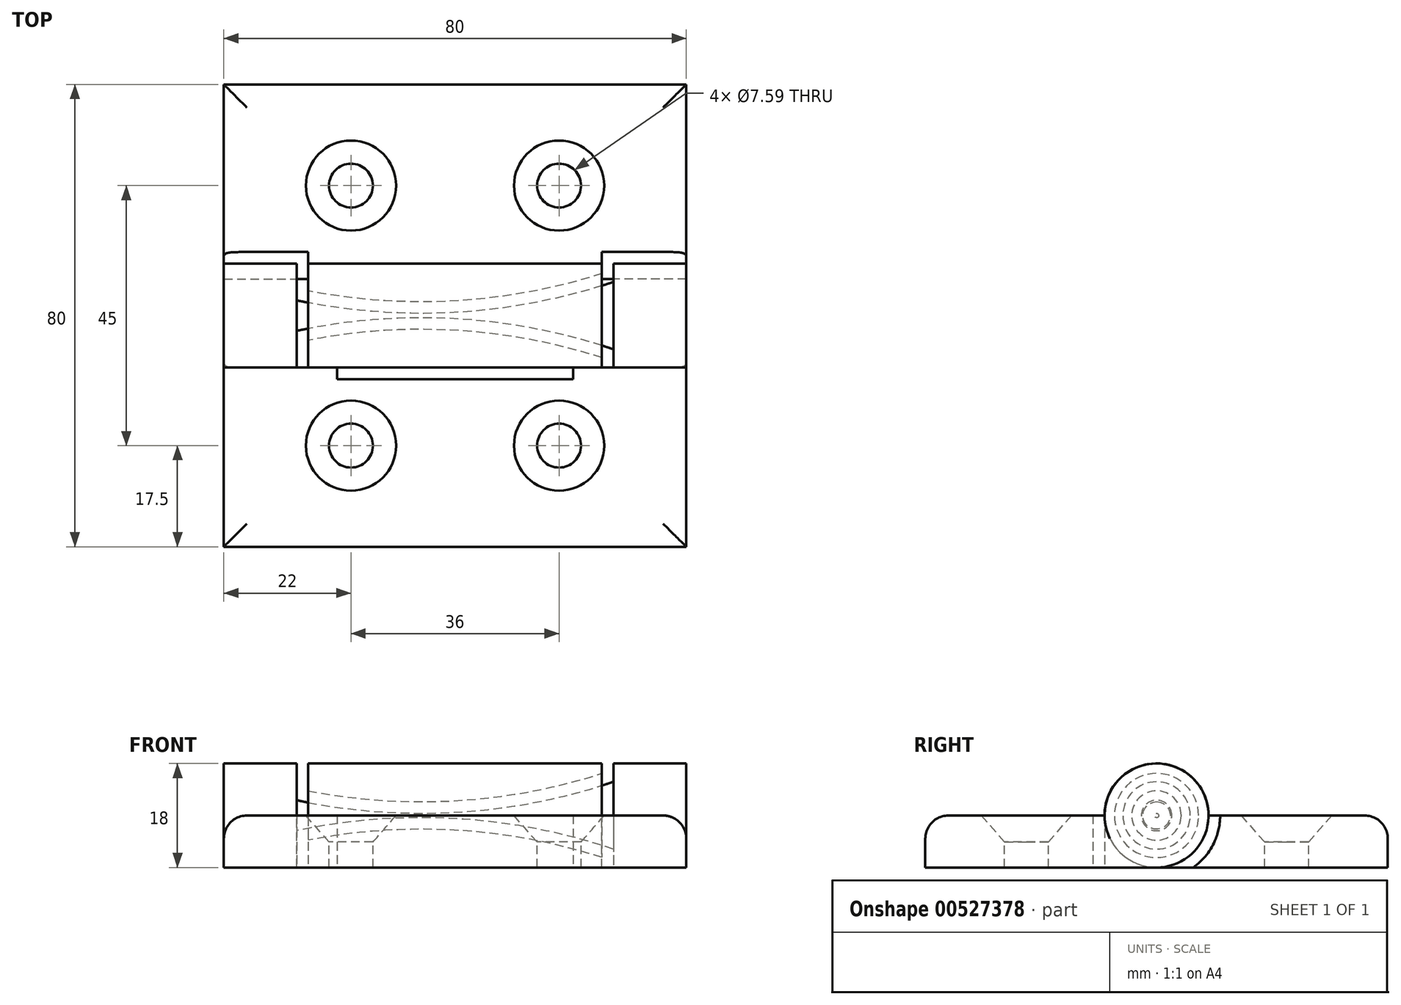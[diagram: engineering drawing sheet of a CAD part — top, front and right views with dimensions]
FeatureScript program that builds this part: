
annotation { "Feature Type Name" : "Feature", "Feature Type Description" : "" }
export const myFeature = defineFeature(function(context is Context, id is Id, definition is map)
    precondition{}
    {
        {
            var Q0;
            Q0=qCreatedBy(makeId("Front.planeOp"),FACE);
            var sketch = newSketch(context, id + "F0", { "sketchPlane" : qUnion([Q0])});
            skLineSegment(sketch, "E0", {"start": v(-18.48, 0) * mm, "end": v(18.23, 0) * mm, "construction": true});
            skLineSegment(sketch, "E1", {"start": v(-12.7, 18.4) * mm, "end": v(-12.7, -18.31) * mm, "construction": true});
            skLineSegment(sketch, "E2", {"start": v(12.7, 18.4) * mm, "end": v(12.7, -18.31) * mm, "construction": true});
            skLineSegment(sketch, "E3.0", {"start": v(-18.48, 2) * mm, "end": v(18.23, 2) * mm, "construction": true});
            skLineSegment(sketch, "E4.0", {"start": v(-18.48, 1) * mm, "end": v(18.48, 1) * mm, "construction": true});
            skPoint(sketch, "E5", {"position": v(0, 1) * mm});
            skPoint(sketch, "E6", {"position": v(12.7, 2) * mm});
            skPoint(sketch, "E7", {"position": v(-12.7, 2) * mm});
            skArc(sketch, "E8", {"start": v(-12.7, 2) * mm, "mid": v(0, 1) * mm, "end": v(12.7, 2) * mm});
            skLineSegment(sketch, "E9", {"start": v(-12.7, 2) * mm, "end": v(-12.7, 0) * mm});
            skLineSegment(sketch, "E10", {"start": v(-12.7, 0) * mm, "end": v(12.7, 0) * mm});
            skLineSegment(sketch, "E11", {"start": v(12.7, 0) * mm, "end": v(12.7, 2) * mm});
            skSolve(sketch);
        }
        {
            var Q0;
            Q0=qCreatedBy(makeId("Front.planeOp"),FACE);
            var sketch = newSketch(context, id + "F1", { "sketchPlane" : qUnion([Q0])});
            skLineSegment(sketch, "E12.0", {"start": v(-12.7, 0) * mm, "end": v(12.7, 0) * mm});
            skLineSegment(sketch, "E13.0", {"start": v(-12.7, 1.12) * mm, "end": v(-12.7, 0) * mm});
            skLineSegment(sketch, "E14.0", {"start": v(12.7, 0) * mm, "end": v(12.7, 2.59) * mm});
            skLineSegment(sketch, "E15.0", {"start": v(13.7, 0) * mm, "end": v(13.7, 3.97) * mm});
            skArc(sketch, "E15.1", {"start": v(-13.7, 2.34) * mm, "mid": v(0.11, 1.28) * mm, "end": v(13.7, 3.97) * mm});
            skLineSegment(sketch, "E15.2", {"start": v(-13.7, 2.34) * mm, "end": v(-13.7, 0) * mm});
            skLineSegment(sketch, "E16", {"start": v(-13.7, 0) * mm, "end": v(-12.7, 0) * mm});
            skLineSegment(sketch, "E17", {"start": v(-13.7, 2.34) * mm, "end": v(-13.7, 4.5) * mm});
            skLineSegment(sketch, "E18", {"start": v(-13.7, 4.5) * mm, "end": v(13.7, 4.5) * mm});
            skLineSegment(sketch, "E19", {"start": v(13.7, 4.5) * mm, "end": v(13.7, 3.97) * mm});
            skLineSegment(sketch, "E20", {"start": v(-12.7, 2.14) * mm, "end": v(-12.7, 4.5) * mm});
            skLineSegment(sketch, "E21", {"start": v(12.7, 3.64) * mm, "end": v(12.7, 4.5) * mm});
            skArc(sketch, "E22.0", {"start": v(-13.7, 1.32) * mm, "mid": v(0.1, 0.28) * mm, "end": v(13.7, 2.91) * mm});
            skLineSegment(sketch, "E23", {"start": v(-12.7, 2.14) * mm, "end": v(-12.7, 1.12) * mm});
            skLineSegment(sketch, "E24", {"start": v(12.7, 3.64) * mm, "end": v(12.7, 2.59) * mm});
            skLineSegment(sketch, "E25", {"start": v(13.7, 0) * mm, "end": v(12.7, 0) * mm});
            skSolve(sketch);
        }
        {
            var Q0;
            Q0=makeQuery(id+"F1.imprint","IMPRINT",FACE,{"disambiguationData":[TD([[makeQuery(id+"F1.imprint","IMPRINT",EDGE,{"derivedFrom":sQuery(id+"F1.wireOp",EDGE,"E12.0")}),1.0]])]});
            var Q1;
            {var subQ0=sQuery(id+"F1.wireOp",EDGE,"E13.0");Q1=makeQuery(id+"F1.imprint","IMPRINT",FACE,{"disambiguationData":[TD([[makeQuery(id+"F1.imprint","IMPRINT",EDGE,{"derivedFrom":subQ0}),-1.0]])]});}
            var Q2;
            {var subQ0=sQuery(id+"F1.wireOp",EDGE,"E14.0");Q2=makeQuery(id+"F1.imprint","IMPRINT",FACE,{"disambiguationData":[TD([[makeQuery(id+"F1.imprint","IMPRINT",EDGE,{"derivedFrom":subQ0}),-1.0]])]});}
            var Q3;
            Q3=sQuery(id+"F1.wireOp",EDGE,"E12.0");
            revolve(context, id + "F2", {"entities" : qUnion([Q0, Q1, Q2]), "axis" : qUnion([Q3]), "revolveType" : RevolveType.FULL});
        }
        {
            var Q0;
            {var subQ0=sQuery(id+"F1.wireOp",EDGE,"E20");Q0=makeQuery(id+"F1.imprint","IMPRINT",FACE,{"disambiguationData":[TD([[makeQuery(id+"F1.imprint","IMPRINT",EDGE,{"derivedFrom":subQ0}),-1.0]])]});}
            var Q1;
            Q1=sQuery(id+"F1.wireOp",EDGE,"E12.0");
            revolve(context, id + "F3", {"entities" : qUnion([Q0]), "axis" : qUnion([Q1]), "revolveType" : RevolveType.FULL});
        }
        {
            var Q0;
            Q0=qCreatedBy(makeId("Right.planeOp"),FACE);
            var sketch = newSketch(context, id + "F4", { "sketchPlane" : qUnion([Q0])});
            skPoint(sketch, "E26", {"position": v(4.5, 0) * mm});
            skLineSegment(sketch, "E27.0", {"start": v(-20, 18.4) * mm, "end": v(-20, -18.31) * mm, "construction": true});
            skLineSegment(sketch, "E28", {"start": v(-23.98, 0) * mm, "end": v(20, 0) * mm, "construction": true});
            skLineSegment(sketch, "E29.0", {"start": v(-23.98, -4.5) * mm, "end": v(20, -4.5) * mm, "construction": true});
            skPoint(sketch, "E30", {"position": v(-20, 0) * mm});
            skPoint(sketch, "E31", {"position": v(-20, -4.5) * mm});
            skPoint(sketch, "E32", {"position": v(4.5, -4.5) * mm});
            skLineSegment(sketch, "E33", {"start": v(-20, 0) * mm, "end": v(-20, -4.5) * mm});
            skLineSegment(sketch, "E34", {"start": v(4.5, -4.5) * mm, "end": v(4.5, 0) * mm});
            skLineSegment(sketch, "E35", {"start": v(-20, 0) * mm, "end": v(4.5, 0) * mm});
            skLineSegment(sketch, "E36", {"start": v(4.5, -4.5) * mm, "end": v(-20, -4.5) * mm});
            skLineSegment(sketch, "E37.0", {"start": v(20, 18.4) * mm, "end": v(20, -18.31) * mm, "construction": true});
            skPoint(sketch, "E38", {"position": v(-4.5, 0) * mm});
            skPoint(sketch, "E39", {"position": v(-20.6, 23.68) * mm});
            skLineSegment(sketch, "E40", {"start": v(-4.5, 0) * mm, "end": v(-4.5, -4.5) * mm});
            skLineSegment(sketch, "E41", {"start": v(4.5, 0) * mm, "end": v(20, 0) * mm});
            skLineSegment(sketch, "E42", {"start": v(20, -4.5) * mm, "end": v(20, 0) * mm});
            skLineSegment(sketch, "E43", {"start": v(20, -4.5) * mm, "end": v(4.5, -4.5) * mm});
            skCircle(sketch, "E44.0", {"center": v(0, 0) * mm, "radius": 4.5 * mm});
            skSolve(sketch);
        }
        {
            var Q0;
            Q0=qCreatedBy(makeId("Right.planeOp"),FACE);
            cPlane(context, id + "F5", {"entities" : qUnion([Q0]), "cplaneType" : CPlaneType.OFFSET, "offset" : 20 * mm, "width" : 150 * mm, "height" : 150 * mm});
        }
        {
            var Q0;
            Q0=qCreatedBy(makeId("Right.planeOp"),FACE);
            cPlane(context, id + "F6", {"entities" : qUnion([Q0]), "cplaneType" : CPlaneType.OFFSET, "offset" : 20 * mm, "oppositeDirection" : true, "width" : 150 * mm, "height" : 150 * mm});
        }
        {
            var Q0;
            Q0=makeQuery(id+"F4.imprint","IMPRINT",FACE,{"disambiguationData":[TD([[makeQuery(id+"F4.imprint","IMPRINT",EDGE,{"derivedFrom":sQuery(id+"F4.wireOp",EDGE,"E34")}),-1.0]])]});
            var Q1;
            {var subQ0=sQuery(id+"F4.wireOp",EDGE,"E34");Q1=makeQuery(id+"F4.imprint","IMPRINT",FACE,{"disambiguationData":[TD([[makeQuery(id+"F4.imprint","IMPRINT",EDGE,{"derivedFrom":subQ0}),1.0]])]});}
            var Q2;
            Q2=makeQuery(id+"F3.opRevolve","SWEPT_FACE",FACE,{"disambiguationData":[OSD([sQuery(id+"F1.wireOp",EDGE,"E21")])]});
            var Q3;
            Q3=makeQuery(id+"F3.opRevolve","SWEPT_FACE",FACE,{"disambiguationData":[OSD([sQuery(id+"F1.wireOp",EDGE,"E20")])]});
            extrude(context, id + "F7", {"entities" : qUnion([Q0, Q1]), "operationType" : NewBodyOperationType.ADD, "endBound" : BoundingType.UP_TO_SURFACE, "endBoundEntityFace" : qUnion([Q2]), "depth" : 25 * mm, "hasSecondDirection" : true, "secondDirectionBound" : SecondDirectionBoundingType.UP_TO_SURFACE, "secondDirectionOppositeDirection" : true, "secondDirectionBoundEntityFace" : qUnion([Q3]), "secondDirectionDepth" : 25 * mm});
        }
        {
            var Q0;
            Q0=qCreatedBy(id+"F5.planeOp",FACE);
            var sketch = newSketch(context, id + "F8", { "sketchPlane" : qUnion([Q0])});
            skLineSegment(sketch, "E45.0", {"start": v(-20, 0) * mm, "end": v(4.5, 0) * mm});
            skLineSegment(sketch, "E46.0", {"start": v(-4.5, 0) * mm, "end": v(-4.5, -4.5) * mm});
            skLineSegment(sketch, "E47.0", {"start": v(4.5, -4.5) * mm, "end": v(-20, -4.5) * mm});
            skLineSegment(sketch, "E48.0", {"start": v(-20, 0) * mm, "end": v(-20, -4.5) * mm});
            skCircle(sketch, "E49.0", {"center": v(0, 0) * mm, "radius": 4.5 * mm});
            skLineSegment(sketch, "E50.0", {"start": v(-5.5, 0) * mm, "end": v(-5.5, -4.5) * mm});
            skSolve(sketch);
        }
        {
            var Q0;
            {var subQ0=sQuery(id+"F8.wireOp",EDGE,"E49.0");var subQ1=sQuery(id+"F8.wireOp",EDGE,"E45.0");var subQ2=makeQuery(id+"F8.imprint","INTERSECT",VERTEX,{"derivedFrom":[subQ1,subQ0]});Q0=makeQuery(id+"F8.imprint","IMPRINT",FACE,{"disambiguationData":[TD([[makeQuery(id+"F8.imprint","IMPRINT",EDGE,{"disambiguationData":[TD([[subQ2,1.0]])],"derivedFrom":subQ1}),1.0]])]});}
            var Q1;
            {var subQ0=sQuery(id+"F8.wireOp",EDGE,"E49.0");var subQ1=sQuery(id+"F8.wireOp",EDGE,"E45.0");var subQ2=makeQuery(id+"F8.imprint","INTERSECT",VERTEX,{"derivedFrom":[subQ1,subQ0]});Q1=makeQuery(id+"F8.imprint","IMPRINT",FACE,{"disambiguationData":[TD([[makeQuery(id+"F8.imprint","IMPRINT",EDGE,{"disambiguationData":[TD([[subQ2,1.0]])],"derivedFrom":subQ0}),1.0]])]});}
            var Q2;
            {var subQ0=sQuery(id+"F8.wireOp",EDGE,"E46.0");Q2=makeQuery(id+"F8.imprint","IMPRINT",FACE,{"disambiguationData":[TD([[makeQuery(id+"F8.imprint","IMPRINT",EDGE,{"derivedFrom":subQ0}),1.0]])]});}
            var Q3;
            Q3=makeQuery(id+"F2.opRevolve","SWEPT_FACE",FACE,{"disambiguationData":[OSD([sQuery(id+"F1.wireOp",EDGE,"E15.0")])]});
            extrude(context, id + "F9", {"entities" : qUnion([Q0, Q1, Q2]), "operationType" : NewBodyOperationType.ADD, "endBound" : BoundingType.UP_TO_SURFACE, "oppositeDirection" : true, "endBoundEntityFace" : qUnion([Q3]), "depth" : 25 * mm});
        }
        {
            var Q0;
            Q0=qCreatedBy(id+"F6.planeOp",FACE);
            var sketch = newSketch(context, id + "F10", { "sketchPlane" : qUnion([Q0])});
            skCircle(sketch, "E51.0", {"center": v(0, 0) * mm, "radius": 4.5 * mm});
            skLineSegment(sketch, "E52.0", {"start": v(4.5, -4.5) * mm, "end": v(-20, -4.5) * mm});
            skLineSegment(sketch, "E53.0", {"start": v(-4.5, 0) * mm, "end": v(-4.5, -4.5) * mm});
            skLineSegment(sketch, "E54.0", {"start": v(-20, 0) * mm, "end": v(-20, -4.5) * mm});
            skLineSegment(sketch, "E55.0", {"start": v(-20, 0) * mm, "end": v(4.5, 0) * mm});
            skLineSegment(sketch, "E56.0", {"start": v(-5.5, 0) * mm, "end": v(-5.5, -4.5) * mm});
            skSolve(sketch);
        }
        {
            var Q0;
            {var subQ0=sQuery(id+"F10.wireOp",EDGE,"E55.0");var subQ1=sQuery(id+"F10.wireOp",EDGE,"E51.0");var subQ2=makeQuery(id+"F10.imprint","INTERSECT",VERTEX,{"derivedFrom":[subQ1,subQ0]});Q0=makeQuery(id+"F10.imprint","IMPRINT",FACE,{"disambiguationData":[TD([[makeQuery(id+"F10.imprint","IMPRINT",EDGE,{"disambiguationData":[TD([[subQ2,1.0]])],"derivedFrom":subQ1}),1.0]])]});}
            var Q1;
            {var subQ0=sQuery(id+"F10.wireOp",EDGE,"E55.0");var subQ1=sQuery(id+"F10.wireOp",EDGE,"E51.0");var subQ3=makeQuery(id+"F10.imprint","INTERSECT",VERTEX,{"derivedFrom":[subQ1,subQ0]});Q1=makeQuery(id+"F10.imprint","IMPRINT",FACE,{"disambiguationData":[TD([[makeQuery(id+"F10.imprint","IMPRINT",EDGE,{"disambiguationData":[TD([[subQ3,-1.0]])],"derivedFrom":subQ1}),1.0]])]});}
            var Q2;
            {var subQ0=sQuery(id+"F10.wireOp",EDGE,"E53.0");Q2=makeQuery(id+"F10.imprint","IMPRINT",FACE,{"disambiguationData":[TD([[makeQuery(id+"F10.imprint","IMPRINT",EDGE,{"derivedFrom":subQ0}),1.0]])]});}
            var Q3;
            Q3=makeQuery(id+"F2.opRevolve","SWEPT_FACE",FACE,{"disambiguationData":[OSD([sQuery(id+"F1.wireOp",EDGE,"E15.2")])]});
            extrude(context, id + "F11", {"entities" : qUnion([Q0, Q1, Q2]), "operationType" : NewBodyOperationType.ADD, "endBound" : BoundingType.UP_TO_SURFACE, "endBoundEntityFace" : qUnion([Q3]), "depth" : 25 * mm});
        }
        {
            var Q0;
            {var subQ0=sQuery(id+"F8.wireOp",EDGE,"E46.0");Q0=makeQuery(id+"F8.imprint","IMPRINT",FACE,{"disambiguationData":[TD([[makeQuery(id+"F8.imprint","IMPRINT",EDGE,{"derivedFrom":subQ0}),-1.0]])]});}
            var Q1;
            Q1=makeQuery(id+"F14.opExtrude","SWEPT_FACE",FACE,{"disambiguationData":[OSD([sQuery(id+"F8.wireOp",EDGE,"E50.0")])]});
            extrude(context, id + "F12", {"entities" : qUnion([Q0]), "operationType" : NewBodyOperationType.ADD, "oppositeDirection" : true, "endBoundEntityFace" : qUnion([Q1]), "depth" : (10 - .2) * mm});
        }
        {
            var Q0;
            {var subQ0=sQuery(id+"F10.wireOp",EDGE,"E53.0");Q0=makeQuery(id+"F10.imprint","IMPRINT",FACE,{"disambiguationData":[TD([[makeQuery(id+"F10.imprint","IMPRINT",EDGE,{"derivedFrom":subQ0}),-1.0]])]});}
            extrude(context, id + "F13", {"entities" : qUnion([Q0]), "operationType" : NewBodyOperationType.ADD, "depth" : (10 - .2) * mm});
        }
        {
            var Q0;
            {var subQ0=sQuery(id+"F8.wireOp",EDGE,"E48.0");Q0=makeQuery(id+"F8.imprint","IMPRINT",FACE,{"disambiguationData":[TD([[makeQuery(id+"F8.imprint","IMPRINT",EDGE,{"derivedFrom":subQ0}),1.0]])]});}
            var Q1;
            {var subQ0=sQuery(id+"F10.wireOp",EDGE,"E53.0");var subQ1=sQuery(id+"F10.wireOp",EDGE,"E52.0");Q1=makeQuery(id+"F13.boolean.opBoolean","MERGE",FACE,{"derivedFrom":[makeQuery(id+"F11.opExtrude","CAP_FACE",FACE,{"disambiguationData":[OSD([sQuery(id+"F10.wireOp",EDGE,"E51.0"),subQ1,subQ0])],"isStart":true}),makeQuery(id+"F13.opExtrude","CAP_FACE",FACE,{"disambiguationData":[OSD([subQ1,subQ0,sQuery(id+"F10.wireOp",EDGE,"E55.0"),sQuery(id+"F10.wireOp",EDGE,"E56.0")])],"isStart":true})]});}
            extrude(context, id + "F14", {"entities" : qUnion([Q0]), "operationType" : NewBodyOperationType.ADD, "endBound" : BoundingType.UP_TO_SURFACE, "oppositeDirection" : true, "endBoundEntityFace" : qUnion([Q1]), "depth" : 40 * mm});
        }
        {
            var Q0;
            Q0=makeQuery(id+"F7.boolean.opBoolean","MERGE",FACE,{"derivedFrom":[makeQuery(id+"F3.opRevolve","SWEPT_FACE",FACE,{"disambiguationData":[OSD([sQuery(id+"F1.wireOp",EDGE,"E20")])]}),makeQuery(id+"F7.opExtrude","CAP_FACE",FACE,{"disambiguationData":[OSD([sQuery(id+"F4.wireOp",EDGE,"E36"),sQuery(id+"F4.wireOp",EDGE,"E41"),sQuery(id+"F4.wireOp",EDGE,"E42"),sQuery(id+"F4.wireOp",EDGE,"E43"),sQuery(id+"F4.wireOp",EDGE,"E44.0")])],"isStart":true})]});
            var sketch = newSketch(context, id + "F15", { "sketchPlane" : qUnion([Q0])});
            skCircle(sketch, "E57.0", {"center": v(0, 0) * mm, "radius": 5.5 * mm});
            skSolve(sketch);
        }
        {
            var Q0;
            {var subQ5=makeQuery(id+"F7.opExtrude","CAP_EDGE",EDGE,{"disambiguationData":[OSD([sQuery(id+"F4.wireOp",EDGE,"E42")])],"isStart":true});Q0=makeQuery(id+"F15.imprint","IMPRINT",FACE,{"disambiguationData":[TD([[makeQuery(id+"F15.imprint","IMPRINT",EDGE,{"derivedFrom":subQ5}),1.0]])]});}
            var Q1;
            {var subQ0=sQuery(id+"F10.wireOp",EDGE,"E53.0");var subQ1=sQuery(id+"F10.wireOp",EDGE,"E52.0");Q1=makeQuery(id+"F14.boolean.opBoolean","MERGE",FACE,{"derivedFrom":[makeQuery(id+"F13.boolean.opBoolean","MERGE",FACE,{"derivedFrom":[makeQuery(id+"F11.opExtrude","CAP_FACE",FACE,{"disambiguationData":[OSD([sQuery(id+"F10.wireOp",EDGE,"E51.0"),subQ1,subQ0])],"isStart":true}),makeQuery(id+"F13.opExtrude","CAP_FACE",FACE,{"disambiguationData":[OSD([subQ1,subQ0,sQuery(id+"F10.wireOp",EDGE,"E55.0"),sQuery(id+"F10.wireOp",EDGE,"E56.0")])],"isStart":true})]}),makeQuery(id+"F14.opExtrude","CAP_FACE",FACE,{"disambiguationData":[OSD([sQuery(id+"F8.wireOp",EDGE,"E45.0"),sQuery(id+"F8.wireOp",EDGE,"E47.0"),sQuery(id+"F8.wireOp",EDGE,"E48.0"),sQuery(id+"F8.wireOp",EDGE,"E50.0")])],"isStart":false})]});}
            extrude(context, id + "F16", {"entities" : qUnion([Q0]), "operationType" : NewBodyOperationType.ADD, "endBound" : BoundingType.UP_TO_SURFACE, "endBoundEntityFace" : qUnion([Q1]), "depth" : 25 * mm});
        }
        {
            var Q0;
            Q0=makeQuery(id+"F7.boolean.opBoolean","MERGE",FACE,{"derivedFrom":[makeQuery(id+"F3.opRevolve","SWEPT_FACE",FACE,{"disambiguationData":[OSD([sQuery(id+"F1.wireOp",EDGE,"E21")])]}),makeQuery(id+"F7.opExtrude","CAP_FACE",FACE,{"disambiguationData":[OSD([sQuery(id+"F4.wireOp",EDGE,"E36"),sQuery(id+"F4.wireOp",EDGE,"E41"),sQuery(id+"F4.wireOp",EDGE,"E42"),sQuery(id+"F4.wireOp",EDGE,"E43"),sQuery(id+"F4.wireOp",EDGE,"E44.0")])],"isStart":false})]});
            var sketch = newSketch(context, id + "F17", { "sketchPlane" : qUnion([Q0])});
            skCircle(sketch, "E58.0", {"center": v(0, 0) * mm, "radius": 5.5 * mm});
            skSolve(sketch);
        }
        {
            var Q0;
            {var subQ5=makeQuery(id+"F7.opExtrude","CAP_EDGE",EDGE,{"disambiguationData":[OSD([sQuery(id+"F4.wireOp",EDGE,"E42")])],"isStart":false});Q0=makeQuery(id+"F17.imprint","IMPRINT",FACE,{"disambiguationData":[TD([[makeQuery(id+"F17.imprint","IMPRINT",EDGE,{"derivedFrom":subQ5}),-1.0]])]});}
            var Q1;
            {var subQ0=sQuery(id+"F8.wireOp",EDGE,"E50.0");var subQ1=sQuery(id+"F8.wireOp",EDGE,"E47.0");var subQ2=sQuery(id+"F8.wireOp",EDGE,"E45.0");var subQ3=sQuery(id+"F8.wireOp",EDGE,"E46.0");Q1=makeQuery(id+"F14.boolean.opBoolean","MERGE",FACE,{"derivedFrom":[makeQuery(id+"F12.boolean.opBoolean","MERGE",FACE,{"derivedFrom":[makeQuery(id+"F9.opExtrude","CAP_FACE",FACE,{"disambiguationData":[OSD([subQ3,subQ1,sQuery(id+"F8.wireOp",EDGE,"E49.0")])],"isStart":true}),makeQuery(id+"F12.opExtrude","CAP_FACE",FACE,{"disambiguationData":[OSD([subQ2,subQ3,subQ1,subQ0])],"isStart":true})]}),makeQuery(id+"F14.opExtrude","CAP_FACE",FACE,{"disambiguationData":[OSD([subQ2,subQ1,sQuery(id+"F8.wireOp",EDGE,"E48.0"),subQ0])],"isStart":true})]});}
            extrude(context, id + "F18", {"entities" : qUnion([Q0]), "operationType" : NewBodyOperationType.ADD, "endBound" : BoundingType.UP_TO_SURFACE, "endBoundEntityFace" : qUnion([Q1]), "depth" : 25 * mm, "offsetDistance" : 25 * mm});
        }
        {
            var Q0;
            Q0=makeQuery(id+"F14.opExtrude","CAP_EDGE",EDGE,{"disambiguationData":[OSD([sQuery(id+"F4.wireOp",EDGE,"E35")])],"isStart":true});
            var Q1;
            Q1=makeQuery(id+"F14.opExtrude","SWEPT_EDGE",EDGE,{"disambiguationData":[OSD([sQuery(id+"F4.wireOp",EDGE,"E33"),sQuery(id+"F4.wireOp",EDGE,"E35")])]});
            var Q2;
            Q2=makeQuery(id+"F14.opExtrude","CAP_EDGE",EDGE,{"disambiguationData":[OSD([sQuery(id+"F4.wireOp",EDGE,"E35")])],"isStart":false});
            var Q3;
            Q3=makeQuery(id+"F18.opExtrude","CAP_EDGE",EDGE,{"disambiguationData":[OSD([sQuery(id+"F4.wireOp",EDGE,"E41")])],"isStart":false});
            var Q4;
            {var subQ0=sQuery(id+"F4.wireOp",EDGE,"E42");var subQ1=sQuery(id+"F4.wireOp",EDGE,"E41");Q4=makeQuery(id+"F18.boolean.opBoolean","MERGE",EDGE,{"derivedFrom":[makeQuery(id+"F16.boolean.opBoolean","MERGE",EDGE,{"derivedFrom":[makeQuery(id+"F7.opExtrude","TWEAK_EDGE",EDGE,{"derivedFrom":[makeQuery(id+"F4.imprint","IMPRINT",EDGE,{"derivedFrom":subQ1}),makeQuery(id+"F4.imprint","IMPRINT",EDGE,{"derivedFrom":subQ0})]}),makeQuery(id+"F16.opExtrude","SWEPT_EDGE",EDGE,{"disambiguationData":[OSD([subQ1,subQ0])]})]}),makeQuery(id+"F18.opExtrude","SWEPT_EDGE",EDGE,{"disambiguationData":[OSD([subQ1,subQ0])]})]});}
            var Q5;
            Q5=makeQuery(id+"F16.opExtrude","CAP_EDGE",EDGE,{"disambiguationData":[OSD([sQuery(id+"F4.wireOp",EDGE,"E41")])],"isStart":false});
            var Q6;
            Q6=makeQuery(id+"F14.boolean.opBoolean","MERGE",EDGE,{"derivedFrom":[makeQuery(id+"F13.opExtrude","CAP_EDGE",EDGE,{"disambiguationData":[OSD([sQuery(id+"F10.wireOp",EDGE,"E55.0")])],"isStart":true}),makeQuery(id+"F14.opExtrude","CAP_EDGE",EDGE,{"disambiguationData":[OSD([sQuery(id+"F8.wireOp",EDGE,"E45.0")])],"isStart":false})]});
            var Q7;
            Q7=makeQuery(id+"F14.opExtrude","SWEPT_EDGE",EDGE,{"disambiguationData":[OSD([sQuery(id+"F8.wireOp",EDGE,"E45.0"),sQuery(id+"F8.wireOp",EDGE,"E48.0")])]});
            var Q8;
            {var subQ0=sQuery(id+"F8.wireOp",EDGE,"E45.0");Q8=makeQuery(id+"F14.boolean.opBoolean","MERGE",EDGE,{"derivedFrom":[makeQuery(id+"F12.opExtrude","CAP_EDGE",EDGE,{"disambiguationData":[OSD([subQ0])],"isStart":true}),makeQuery(id+"F14.opExtrude","CAP_EDGE",EDGE,{"disambiguationData":[OSD([subQ0])],"isStart":true})]});}
            fillet(context, id + "F19", {"entities" : qUnion([Q0, Q1, Q2, Q3, Q4, Q5, Q6, Q7, Q8]), "radius" : 2 * mm, "allowEdgeOverflow" : false});
        }
        {
            var Q0;
            {var subQ0=sQuery(id+"F8.wireOp",EDGE,"E45.0");Q0=makeQuery(id+"F14.boolean.opBoolean","MERGE",FACE,{"derivedFrom":[makeQuery(id+"F12.opExtrude","SWEPT_FACE",FACE,{"disambiguationData":[OSD([subQ0])]}),makeQuery(id+"F13.opExtrude","SWEPT_FACE",FACE,{"disambiguationData":[OSD([sQuery(id+"F10.wireOp",EDGE,"E55.0")])]}),makeQuery(id+"F14.opExtrude","SWEPT_FACE",FACE,{"disambiguationData":[OSD([subQ0])]})]});}
            var sketch = newSketch(context, id + "F20", { "sketchPlane" : qUnion([Q0])});
            skLineSegment(sketch, "E59.0", {"start": v(-18, -4.5) * mm, "end": v(-18, -18) * mm});
            skLineSegment(sketch, "E60.0", {"start": v(-18, 18) * mm, "end": v(-18, 5.5) * mm});
            skLineSegment(sketch, "E61.0", {"start": v(-20, 20) * mm, "end": v(20, 20) * mm});
            skLineSegment(sketch, "E62.0", {"start": v(12.7, 4.5) * mm, "end": v(-12.7, 4.5) * mm});
            skLineSegment(sketch, "E63.0", {"start": v(-10.2, -5.5) * mm, "end": v(10.2, -5.5) * mm});
            skLineSegment(sketch, "E64.0", {"start": v(18, 18) * mm, "end": v(-18, 18) * mm});
            skLineSegment(sketch, "E65", {"start": v(9, 4.5) * mm, "end": v(9, 18) * mm, "construction": true});
            skPoint(sketch, "E66.startSnap0", {"position": v(0, 18) * mm});
            skLineSegment(sketch, "E67.0", {"start": v(18, 5.5) * mm, "end": v(18, 18) * mm});
            skLineSegment(sketch, "E68", {"start": v(0, 11.25) * mm, "end": v(18, 11.25) * mm, "construction": true});
            skPoint(sketch, "E68.startSnap0", {"position": v(9, 11.25) * mm});
            skPoint(sketch, "E69.MirrorP", {"position": v(-9, 11.25) * mm});
            skPoint(sketch, "E70.MirrorP", {"position": v(-9, -11.25) * mm});
            skPoint(sketch, "E71.MirrorP", {"position": v(9, -11.25) * mm});
            skSolve(sketch);
        }
        {
            var Q0;
            Q0=sQuery(id+"F20.wireOp",VERTEX,"E68.startSnap0");
            var Q1;
            Q1=sQuery(id+"F20.wireOp",VERTEX,"E69.MirrorP");
            var Q2;
            Q2=sQuery(id+"F20.wireOp",VERTEX,"E70.MirrorP");
            var Q3;
            Q3=sQuery(id+"F20.wireOp",VERTEX,"E71.MirrorP");
            var Q4;
            Q4=makeQuery(id+"F2.opRevolve","SWEPT_BODY",BODY,{"disambiguationData":[OSD([sQuery(id+"F1.wireOp",EDGE,"E12.0"),sQuery(id+"F1.wireOp",EDGE,"E15.0"),sQuery(id+"F1.wireOp",EDGE,"E15.2"),sQuery(id+"F1.wireOp",EDGE,"E16"),sQuery(id+"F1.wireOp",EDGE,"E22.0"),sQuery(id+"F1.wireOp",EDGE,"E25")])]});
            var Q5;
            Q5=makeQuery(id+"F3.opRevolve","SWEPT_BODY",BODY,{"disambiguationData":[OSD([sQuery(id+"F1.wireOp",EDGE,"E15.1"),sQuery(id+"F1.wireOp",EDGE,"E18"),sQuery(id+"F1.wireOp",EDGE,"E20"),sQuery(id+"F1.wireOp",EDGE,"E21")])]});
            hole(context, id + "F21", {"style" : HoleStyle.C_SINK, "endStyle" : HoleEndStyle.THROUGH, "standardTappedOrClearance" : lookupTablePath({ "standard" : "ANSI", "fit" : "Normal (ASME)", "size" : "#6", "type" : "Clearance" }), "standardBlindInLast" : lookupTablePath({ "fit" : "Free", "standard" : "ANSI", "size" : "#6", "type" : "Clearance" }), "holeDiameter" : 3.8 * mm, "cSinkDiameter" : 7.8 * mm, "cSinkAngle" : 82 * degree, "isTappedThrough" : true, "tappedDepth" : 12 * mm, "tapClearance" : 3, "locations" : qUnion([Q0, Q1, Q2, Q3]), "scope" : qUnion([Q4, Q5])});
        }
        {
            var Q0;
            Q0=makeQuery(id+"F2.opRevolve","SWEPT_BODY",BODY,{"disambiguationData":[OSD([sQuery(id+"F1.wireOp",EDGE,"E12.0"),sQuery(id+"F1.wireOp",EDGE,"E15.0"),sQuery(id+"F1.wireOp",EDGE,"E15.2"),sQuery(id+"F1.wireOp",EDGE,"E16"),sQuery(id+"F1.wireOp",EDGE,"E22.0"),sQuery(id+"F1.wireOp",EDGE,"E25")])]});
            var Q1;
            Q1=makeQuery(id+"F3.opRevolve","SWEPT_BODY",BODY,{"disambiguationData":[OSD([sQuery(id+"F1.wireOp",EDGE,"E15.1"),sQuery(id+"F1.wireOp",EDGE,"E18"),sQuery(id+"F1.wireOp",EDGE,"E20"),sQuery(id+"F1.wireOp",EDGE,"E21")])]});
            var Q2;
            Q2=qCreatedBy(makeId("Origin.pointOp"),VERTEX);
            transform(context, id + "F22", {"entities" : qUnion([Q0, Q1]), "transformType" : TransformType.SCALE_UNIFORMLY, "scale" : 2, "scalePoint" : qUnion([Q2]), "makeCopy" : false});
        }
    });
